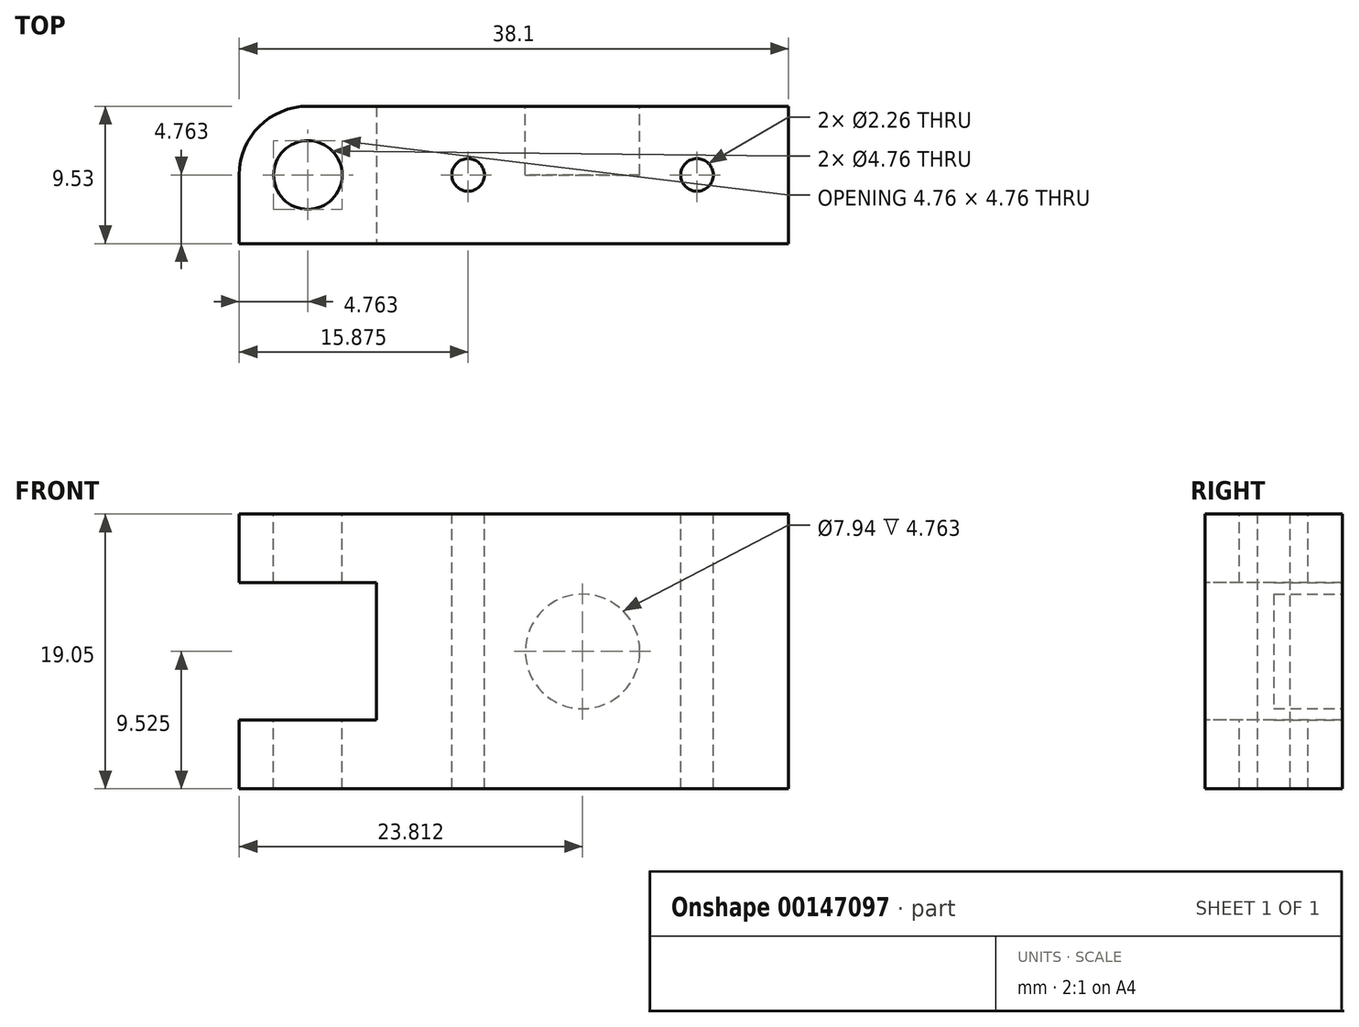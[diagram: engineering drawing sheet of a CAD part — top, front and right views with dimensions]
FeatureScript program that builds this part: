
annotation { "Feature Type Name" : "Feature", "Feature Type Description" : "" }
export const myFeature = defineFeature(function(context is Context, id is Id, definition is map)
    precondition{}
    {
        {
            var Q0;
            Q0=qCreatedBy(makeId("Top.planeOp"),FACE);
            var sketch = newSketch(context, id + "F0", { "sketchPlane" : qUnion([Q0])});
            skLineSegment(sketch, "E0.bottom", {"start": v(0, 0) * mm, "end": v(38.1, 0) * mm});
            skLineSegment(sketch, "E0.top", {"start": v(0, 9.53) * mm, "end": v(38.1, 9.53) * mm});
            skLineSegment(sketch, "E0.left", {"start": v(0, 0) * mm, "end": v(0, 9.53) * mm});
            skLineSegment(sketch, "E0.right", {"start": v(38.1, 0) * mm, "end": v(38.1, 9.53) * mm});
            skSolve(sketch);
        }
        {
            var Q0;
            Q0 = qSketchRegion(id + "F0", true);
            extrude(context, id + "F1", {"entities" : qUnion([Q0]), "depth" : 19.05 * mm});
        }
        {
            var Q0;
            Q0=makeQuery(id+"F1.opExtrude","CAP_FACE",FACE,{"disambiguationData":[OSD([sQuery(id+"F0.wireOp",EDGE,"E0.bottom"),sQuery(id+"F0.wireOp",EDGE,"E0.top"),sQuery(id+"F0.wireOp",EDGE,"E0.left"),sQuery(id+"F0.wireOp",EDGE,"E0.right")])],"isStart":false});
            var sketch = newSketch(context, id + "F2", { "sketchPlane" : qUnion([Q0])});
            skPoint(sketch, "E1", {"position": v(15.88, 4.76) * mm});
            skPoint(sketch, "E2", {"position": v(31.75, 4.76) * mm});
            skLineSegment(sketch, "E3", {"start": v(0, 4.76) * mm, "end": v(15.88, 4.76) * mm});
            skLineSegment(sketch, "E4", {"start": v(15.88, 4.76) * mm, "end": v(31.75, 4.76) * mm});
            skLineSegment(sketch, "E5", {"start": v(31.75, 4.76) * mm, "end": v(38.1, 4.76) * mm});
            skSolve(sketch);
        }
        {
            var Q0;
            Q0=sQuery(id+"F2.wireOp",VERTEX,"E1");
            var Q1;
            Q1=sQuery(id+"F2.wireOp",VERTEX,"E2");
            var Q2;
            Q2=makeQuery(id+"F1.opExtrude","SWEPT_BODY",BODY,{"disambiguationData":[OSD([sQuery(id+"F0.wireOp",EDGE,"E0.bottom"),sQuery(id+"F0.wireOp",EDGE,"E0.top"),sQuery(id+"F0.wireOp",EDGE,"E0.left"),sQuery(id+"F0.wireOp",EDGE,"E0.right")])]});
            hole(context, id + "F3", {"style" : HoleStyle.SIMPLE, "endStyle" : HoleEndStyle.THROUGH, "standardTappedOrClearance" : lookupTablePath({ "standard" : "ANSI", "size" : "#43 (0.09)", "type" : "Drilled" }), "standardBlindInLast" : lookupTablePath({ "standard" : "ANSI", "size" : "#43", "type" : "Drilled" }), "holeDiameter" : 2.26 * mm, "startFromSketch" : true, "locations" : qUnion([Q0, Q1]), "scope" : qUnion([Q2]), "isTappedThrough" : true});
        }
        {
            var Q0;
            Q0=makeQuery(id+"F1.opExtrude","SWEPT_FACE",FACE,{"disambiguationData":[OSD([sQuery(id+"F0.wireOp",EDGE,"E0.bottom")])]});
            var sketch = newSketch(context, id + "F4", { "sketchPlane" : qUnion([Q0])});
            skLineSegment(sketch, "E6.bottom", {"start": v(0, 14.29) * mm, "end": v(9.53, 14.29) * mm});
            skLineSegment(sketch, "E6.top", {"start": v(0, 4.76) * mm, "end": v(9.53, 4.76) * mm});
            skLineSegment(sketch, "E6.left", {"start": v(0, 14.29) * mm, "end": v(0, 4.76) * mm});
            skLineSegment(sketch, "E6.right", {"start": v(9.53, 14.29) * mm, "end": v(9.53, 4.76) * mm});
            skLineSegment(sketch, "E7", {"start": v(0, 19.05) * mm, "end": v(0, 14.29) * mm});
            skLineSegment(sketch, "E8", {"start": v(0, 4.76) * mm, "end": v(0, 0) * mm});
            skSolve(sketch);
        }
        {
            var Q0;
            Q0=makeQuery(id+"F4.imprint","IMPRINT",FACE,{"disambiguationData":[TD([[makeQuery(id+"F4.imprint","IMPRINT",EDGE,{"derivedFrom":sQuery(id+"F4.wireOp",EDGE,"E6.bottom")}),-1.0]])]});
            extrude(context, id + "F5", {"entities" : qUnion([Q0]), "operationType" : NewBodyOperationType.REMOVE, "endBound" : BoundingType.THROUGH_ALL, "oppositeDirection" : true, "depth" : 25.4 * mm});
        }
        {
            var Q0;
            Q0=makeQuery(id+"F1.opExtrude","CAP_FACE",FACE,{"disambiguationData":[OSD([sQuery(id+"F0.wireOp",EDGE,"E0.bottom"),sQuery(id+"F0.wireOp",EDGE,"E0.top"),sQuery(id+"F0.wireOp",EDGE,"E0.left"),sQuery(id+"F0.wireOp",EDGE,"E0.right")])],"isStart":false});
            var sketch = newSketch(context, id + "F6", { "sketchPlane" : qUnion([Q0])});
            skCircle(sketch, "E9", {"center": v(4.76, 4.76) * mm, "radius": 2.38 * mm});
            skLineSegment(sketch, "E10", {"start": v(4.76, 4.76) * mm, "end": v(0, 4.76) * mm});
            skSolve(sketch);
        }
        {
            var Q0;
            Q0=makeQuery(id+"F6.imprint","IMPRINT",FACE,{"disambiguationData":[TD([[makeQuery(id+"F6.imprint","IMPRINT",EDGE,{"derivedFrom":sQuery(id+"F6.wireOp",EDGE,"E9")}),1.0]])]});
            extrude(context, id + "F7", {"entities" : qUnion([Q0]), "operationType" : NewBodyOperationType.REMOVE, "endBound" : BoundingType.THROUGH_ALL, "oppositeDirection" : true, "depth" : 25.4 * mm});
        }
        {
            var Q0;
            {var subQ0=sQuery(id+"F0.wireOp",EDGE,"E0.left");var subQ1=sQuery(id+"F0.wireOp",EDGE,"E0.top");Q0=makeQuery(id+"F5.boolean.opBoolean","SPLIT",EDGE,{"disambiguationData":[TD([makeQuery(id+"F5.opExtrude","SWEPT_FACE",FACE,{"disambiguationData":[OSD([sQuery(id+"F4.wireOp",EDGE,"E6.bottom")])]})])],"derivedFrom":makeQuery(id+"F1.opExtrude","SWEPT_EDGE",EDGE,{"disambiguationData":[OSD([subQ1,subQ0])]})});}
            var Q1;
            {var subQ0=sQuery(id+"F0.wireOp",EDGE,"E0.left");var subQ1=sQuery(id+"F0.wireOp",EDGE,"E0.top");Q1=makeQuery(id+"F5.boolean.opBoolean","SPLIT",EDGE,{"disambiguationData":[TD([makeQuery(id+"F5.opExtrude","SWEPT_FACE",FACE,{"disambiguationData":[OSD([sQuery(id+"F4.wireOp",EDGE,"E6.top")])]})])],"derivedFrom":makeQuery(id+"F1.opExtrude","SWEPT_EDGE",EDGE,{"disambiguationData":[OSD([subQ1,subQ0])]})});}
            fillet(context, id + "F8", {"entities" : qUnion([Q0, Q1]), "radius" : 4.76 * mm, "tangentPropagation" : true, "allowEdgeOverflow" : false});
        }
        {
            var Q0;
            Q0=makeQuery(id+"F1.opExtrude","SWEPT_FACE",FACE,{"disambiguationData":[OSD([sQuery(id+"F0.wireOp",EDGE,"E0.top")])]});
            var sketch = newSketch(context, id + "F9", { "sketchPlane" : qUnion([Q0])});
            skCircle(sketch, "E11", {"center": v(-23.81, 9.53) * mm, "radius": 3.97 * mm});
            skSolve(sketch);
        }
        {
            var Q0;
            Q0 = qSketchRegion(id + "F9", true);
            extrude(context, id + "F10", {"entities" : qUnion([Q0]), "operationType" : NewBodyOperationType.REMOVE, "oppositeDirection" : true, "depth" : 4.76 * mm});
        }
    });
